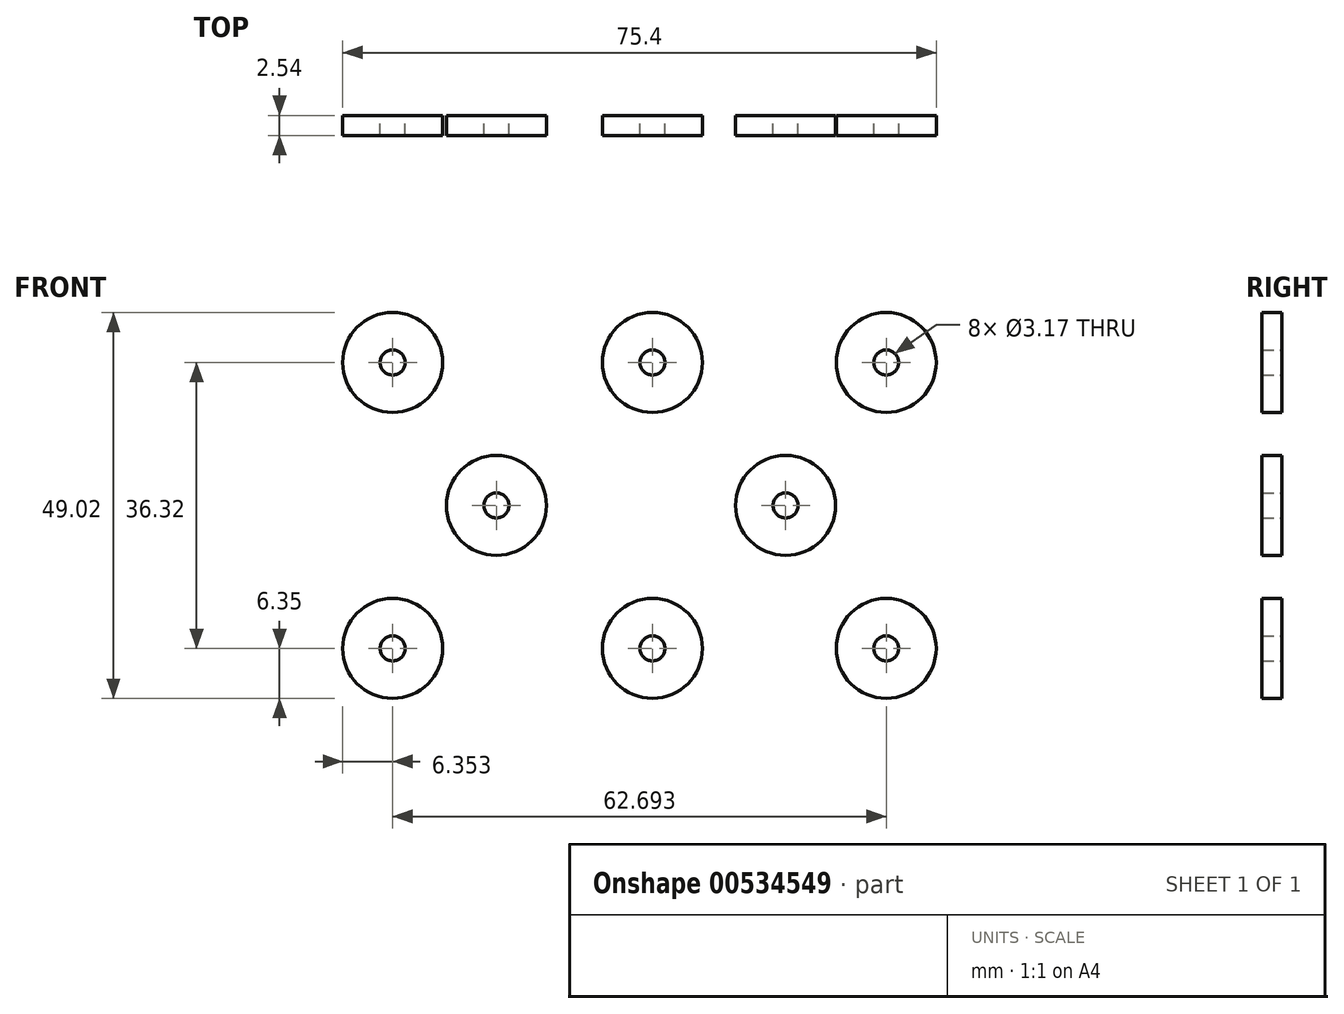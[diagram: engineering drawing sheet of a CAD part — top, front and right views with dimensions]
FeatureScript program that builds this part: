
annotation { "Feature Type Name" : "Feature", "Feature Type Description" : "" }
export const myFeature = defineFeature(function(context is Context, id is Id, definition is map)
    precondition{}
    {
        {
            var Q0;
            Q0=qCreatedBy(makeId("Front.planeOp"),FACE);
            var sketch = newSketch(context, id + "F0", { "sketchPlane" : qUnion([Q0])});
            skCircle(sketch, "E0", {"center": v(-33, 18.16) * mm, "radius": 6.35 * mm});
            skCircle(sketch, "E1", {"center": v(0, 18.16) * mm, "radius": 6.35 * mm});
            skPoint(sketch, "E1.centerSnap0", {"position": v(-1.45, 18.16) * mm});
            skCircle(sketch, "E2", {"center": v(29.7, 18.16) * mm, "radius": 6.35 * mm});
            skCircle(sketch, "E3", {"center": v(-33, 18.16) * mm, "radius": 1.59 * mm});
            skCircle(sketch, "E4", {"center": v(0, 18.16) * mm, "radius": 1.59 * mm});
            skCircle(sketch, "E5", {"center": v(29.7, 18.16) * mm, "radius": 1.59 * mm});
            skCircle(sketch, "E6.MirrorC", {"center": v(-33, -18.16) * mm, "radius": 6.35 * mm});
            skCircle(sketch, "E7.MirrorC", {"center": v(0, -18.16) * mm, "radius": 6.35 * mm});
            skCircle(sketch, "E8.MirrorC", {"center": v(29.7, -18.16) * mm, "radius": 6.35 * mm});
            skCircle(sketch, "E9.MirrorC", {"center": v(0, -18.16) * mm, "radius": 1.59 * mm});
            skCircle(sketch, "E10.MirrorC", {"center": v(29.7, -18.16) * mm, "radius": 1.59 * mm});
            skCircle(sketch, "E11.MirrorC", {"center": v(-33, -18.16) * mm, "radius": 1.59 * mm});
            skCircle(sketch, "E12", {"center": v(-19.82, 0) * mm, "radius": 6.35 * mm});
            skCircle(sketch, "E13", {"center": v(16.92, 0) * mm, "radius": 6.35 * mm});
            skCircle(sketch, "E14", {"center": v(-19.82, 0) * mm, "radius": 1.59 * mm});
            skCircle(sketch, "E15", {"center": v(16.92, 0) * mm, "radius": 1.59 * mm});
            skSolve(sketch);
        }
        {
            var Q0;
            Q0 = qSketchRegion(id + "F0", true);
            extrude(context, id + "F1", {"entities" : qUnion([Q0]), "depth" : 2.54 * mm, "offsetDistance" : 25.4 * mm});
        }
    });
